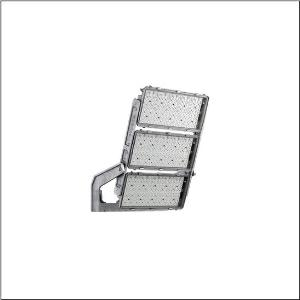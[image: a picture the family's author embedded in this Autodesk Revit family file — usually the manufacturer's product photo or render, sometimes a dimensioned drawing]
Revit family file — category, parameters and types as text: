
# Revit family: floodlight_fl_11_maxi_pro_remote___pl64blc_5xa779427w01aa_301c
name_source: partatom
category: Lighting Fixtures
units: mm (PartAtom-declared; Revit-internal decimal feet)

## family parameters
Cut with Voids When Loaded = No
Host = Face
Light Source = No
Part Type = Normal
Room Calculation Point = No
Round Connector Dimension = Use Diameter
Shared = No

## types (1)
- --- (1 x LED, 142820 lm, 1517.1 W, 5000K)
    Apparent Load = 1517 VA
    CIE Flux Codes = 28 83 99 100 100
    Color Rendering = 70
    Color Temperature = 5000K
    Default Elevation = 1800 mm
    Description = Floodlight FL 11  maxi  pro Remote floodlight; light control with lens of PMMA; cover panel of toughened safety glass, transparent; light distribution: PL64BLC, asymmetric direct distribution, LEDcolour temperature: 5000K, rated luminous flux: 142.820lm, colour rendering: CRI > 70, light colour: 750; luminous efficacy: 94lm/W; brightness control: DALI 2 (1 DALI address); with terminal, 8-pole, max. 2.5mm², mains connection: 220..240V/380..400V AC, 50/60Hz, surge voltage resistance: line to ground: 10kV, ECG replaceable separately, no afterglow with DALI off / DMX off command, LED unit replaceable without ESD environment, dustproof LED module, dimming range 10..100%; 1517W floodlight with 2x LED unit of diecast aluminium, coated grey; length: 713mm / width: 651mm / height: 338mm; mounting bracket, of diecast aluminium, uncoated, natural, equipment: Power, protection rating (complete): IP66; insulation class (complete): insulation class I (protective earthing); certification: CE, ENEC, VDE; ball protection: ball impact resistance with accessories, impact resistance: IK07; only for outdoor installations, rated ambient temperature 10°C, permissible operating ambient temperature: -40..+30°C, permissible storage temperature: -40..+85°C; packaging unit: 1 piece

Light Distribution: PL64BLC
    Height = 320 mm
    Lamp = 1 x LED
    Lamp Light Flux = 142820 lm
    Lamp Power = 1517.1 W
    Lamp count = 1
    Length = 1002 mm
    Luminous efficacy = 94 lm/W
    Manufacturer = Siteco
    ModVariant = No
    Model = 5XA779427W01AA
    Mounting Place = Ceiling
    Mounting Type = Surface mounted
    Number of Poles = 1
    OnlyDefault = Yes
    Power Factor = 1
    Product Name = Floodlight FL 11 maxi pro Remote | PL64BLC
    Product group = floodlight | ceiling mounted
    ProductGroupID = 302
    Protection Class = Protection class I
    Protection Degree = IP 66
    RLX_Detail_Level = 1
    RLX_Emergency_Light_Flux = 0 lm
    RLX_Emergency_Type = 0
    RLX_Emergency_Type_DB = No
    RlxData = <blob elided: 52197 chars, md5=b96c9925>
    Socket = socket
    Standby Power = 0 W
    System Light Flux = 142820 lm
    System Power = 1517 W
    Type Comments = factory setting: luminous flux: 100 % | dim-lin: 254 | 1070 mA
    Type Image = l_1006784.jpg
    URL = http://relux.com
    VarID = @adj_050183
    Voltage = 0 V
    Weight = 0.00 kg
    Width = 655 mm

## geometry (parser evidence)
native form markers: Blend x4, Sweep x13
no freeform markers — native parametric forms only
